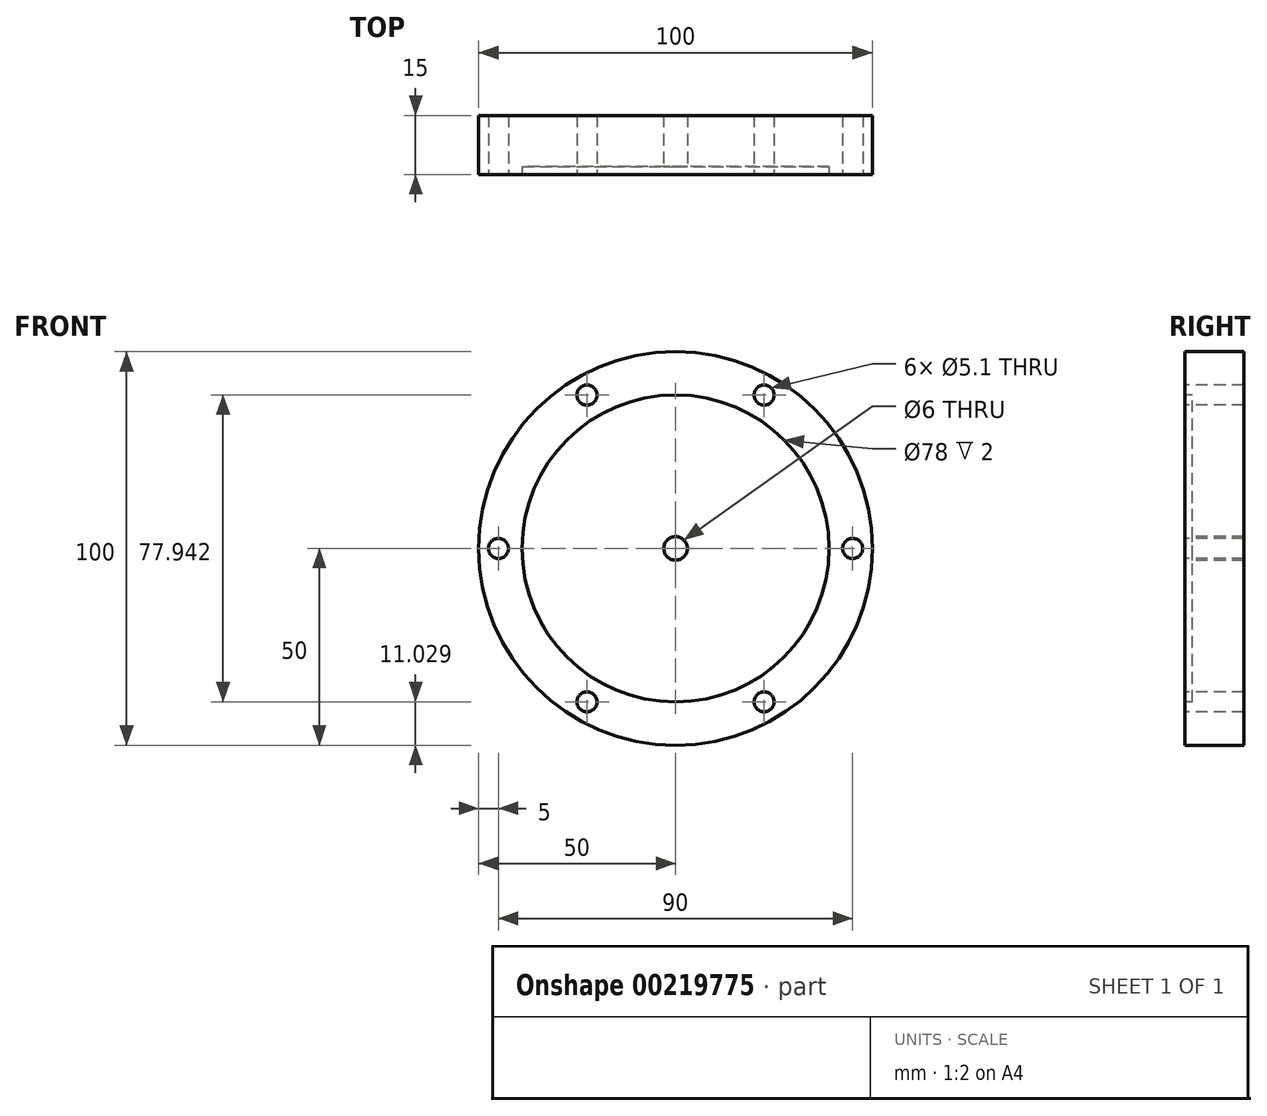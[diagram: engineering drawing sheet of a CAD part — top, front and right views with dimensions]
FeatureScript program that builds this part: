
annotation { "Feature Type Name" : "Feature", "Feature Type Description" : "" }
export const myFeature = defineFeature(function(context is Context, id is Id, definition is map)
    precondition{}
    {
        {
            var Q0;
            Q0=qCreatedBy(makeId("Front.planeOp"),FACE);
            var sketch = newSketch(context, id + "F0", { "sketchPlane" : qUnion([Q0])});
            skCircle(sketch, "E0", {"center": v(0, 0) * mm, "radius": 50 * mm});
            skCircle(sketch, "E1", {"center": v(0, 0) * mm, "radius": 3 * mm});
            skSolve(sketch);
        }
        {
            var Q0;
            Q0 = qSketchRegion(id + "F0", true);
            extrude(context, id + "F1", {"entities" : qUnion([Q0]), "oppositeDirection" : true, "depth" : 15 * mm});
        }
        {
            var Q0;
            Q0=qCreatedBy(makeId("Front.planeOp"),FACE);
            var sketch = newSketch(context, id + "F2", { "sketchPlane" : qUnion([Q0])});
            skPoint(sketch, "E2", {"position": v(-22.5, 38.97) * mm});
            skCircle(sketch, "E3", {"center": v(0, 0) * mm, "radius": 45 * mm, "construction": true});
            skLineSegment(sketch, "E4", {"start": v(-22.5, 38.97) * mm, "end": v(0, 0) * mm, "construction": true});
            skPoint(sketch, "E5", {"position": v(22.5, 38.97) * mm});
            skPoint(sketch, "E6", {"position": v(45, 0) * mm});
            skPoint(sketch, "E7", {"position": v(22.5, -38.97) * mm});
            skPoint(sketch, "E8", {"position": v(-22.5, -38.97) * mm});
            skPoint(sketch, "E9", {"position": v(-45, 0) * mm});
            skLineSegment(sketch, "E10", {"start": v(-45, 0) * mm, "end": v(0, 0) * mm, "construction": true});
            skLineSegment(sketch, "E11", {"start": v(-22.5, -38.97) * mm, "end": v(0, 0) * mm, "construction": true});
            skLineSegment(sketch, "E12", {"start": v(22.5, -38.97) * mm, "end": v(0, 0) * mm, "construction": true});
            skLineSegment(sketch, "E13", {"start": v(45, 0) * mm, "end": v(0, 0) * mm, "construction": true});
            skLineSegment(sketch, "E14", {"start": v(22.5, 38.97) * mm, "end": v(0, 0) * mm, "construction": true});
            skSolve(sketch);
        }
        {
            var Q0;
            Q0=sQuery(id+"F2.wireOp",VERTEX,"E2");
            var Q1;
            Q1=sQuery(id+"F2.wireOp",VERTEX,"E5");
            var Q2;
            Q2=sQuery(id+"F2.wireOp",VERTEX,"E6");
            var Q3;
            Q3=sQuery(id+"F2.wireOp",VERTEX,"E7");
            var Q4;
            Q4=sQuery(id+"F2.wireOp",VERTEX,"E8");
            var Q5;
            Q5=sQuery(id+"F2.wireOp",VERTEX,"E9");
            var Q6;
            Q6=makeQuery(id+"F1.opExtrude","SWEPT_BODY",BODY,{"disambiguationData":[OSD([sQuery(id+"F0.wireOp",EDGE,"E0")])]});
            hole(context, id + "F3", {"style" : HoleStyle.SIMPLE, "endStyle" : HoleEndStyle.THROUGH, "holeDiameter" : 5.1 * mm, "locations" : qUnion([Q0, Q1, Q2, Q3, Q4, Q5]), "scope" : qUnion([Q6]), "isTappedThrough" : true});
        }
        {
            var Q0;
            Q0=qCreatedBy(makeId("Front.planeOp"),FACE);
            var sketch = newSketch(context, id + "F4", { "sketchPlane" : qUnion([Q0])});
            skCircle(sketch, "E15", {"center": v(0, 0) * mm, "radius": 39 * mm});
            skSolve(sketch);
        }
        {
            var Q0;
            Q0 = qSketchRegion(id + "F4", true);
            extrude(context, id + "F5", {"entities" : qUnion([Q0]), "operationType" : NewBodyOperationType.REMOVE, "oppositeDirection" : true, "depth" : 2 * mm});
        }
    });
